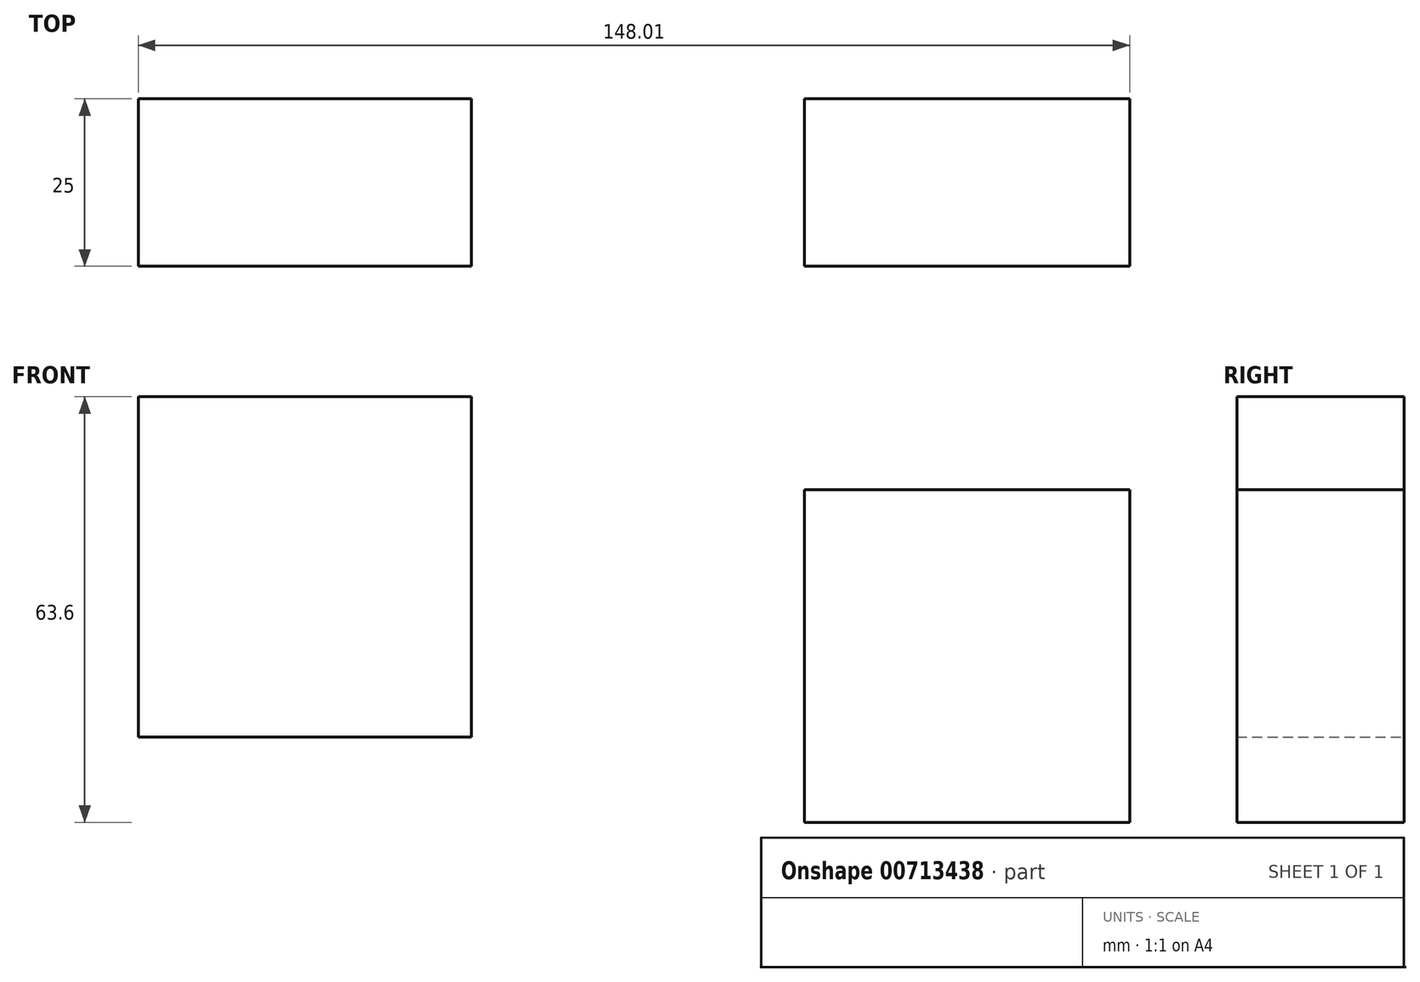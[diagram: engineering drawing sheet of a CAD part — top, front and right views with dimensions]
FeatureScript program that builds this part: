
annotation { "Feature Type Name" : "Feature", "Feature Type Description" : "" }
export const myFeature = defineFeature(function(context is Context, id is Id, definition is map)
    precondition{}
    {
        {
            var Q0;
            Q0=qCreatedBy(makeId("Front.planeOp"),FACE);
            var sketch = newSketch(context, id + "F0", { "sketchPlane" : qUnion([Q0])});
            skLineSegment(sketch, "E0.bottom", {"start": v(-89.47, 16.62) * mm, "end": v(-39.75, 16.62) * mm});
            skLineSegment(sketch, "E0.top", {"start": v(-89.47, 67.5) * mm, "end": v(-39.75, 67.5) * mm});
            skLineSegment(sketch, "E0.left", {"start": v(-89.47, 16.62) * mm, "end": v(-89.47, 67.5) * mm});
            skLineSegment(sketch, "E0.right", {"start": v(-39.75, 16.62) * mm, "end": v(-39.75, 67.5) * mm});
            skPoint(sketch, "E0.middle", {"position": v(-64.6, 42.06) * mm});
            skLineSegment(sketch, "E1.bottom", {"start": v(9.97, 3.9) * mm, "end": v(58.54, 3.9) * mm});
            skLineSegment(sketch, "E1.top", {"start": v(9.97, 53.62) * mm, "end": v(58.54, 53.62) * mm});
            skLineSegment(sketch, "E1.left", {"start": v(9.97, 3.9) * mm, "end": v(9.97, 53.62) * mm});
            skLineSegment(sketch, "E1.right", {"start": v(58.54, 3.9) * mm, "end": v(58.54, 53.62) * mm});
            skPoint(sketch, "E1.middle", {"position": v(34.25, 28.76) * mm});
            skSolve(sketch);
        }
        {
            var Q0;
            Q0=makeQuery(id+"F0.imprint","IMPRINT",FACE,{"disambiguationData":[TD([[makeQuery(id+"F0.imprint","IMPRINT",EDGE,{"derivedFrom":sQuery(id+"F0.wireOp",EDGE,"E0.bottom")}),1.0]])]});
            var Q1;
            Q1=makeQuery(id+"F0.imprint","IMPRINT",FACE,{"disambiguationData":[TD([[makeQuery(id+"F0.imprint","IMPRINT",EDGE,{"derivedFrom":sQuery(id+"F0.wireOp",EDGE,"E1.bottom")}),1.0]])]});
            extrude(context, id + "F1", {"entities" : qUnion([Q0, Q1]), "depth" : 25 * mm, "offsetDistance" : 25 * mm});
        }
    });
